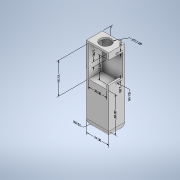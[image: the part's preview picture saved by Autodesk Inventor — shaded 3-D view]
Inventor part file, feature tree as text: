
AUTODESK INVENTOR PART (.ipt)
format: ipt  version: 2022.1 (Build 261234000, 234)  size: 217,088 bytes
history: native  units: mm
features: other x14, extrude x8, sketch x8, fillet x1
ambient origin geometry x8: Origin, YZ Plane, XZ Plane, XY Plane, X Axis, Y Axis, Z Axis, Center Point
bodies: Solid1 (feature_tree)
feature tree (31):
  other  "Annotations"
  extrude  "Extrusion1"  Depth=24.0mm
  extrude  "Extrusion2"  Depth=2.0mm
  extrude  "Extrusion3"  Depth=15.0mm TaperAngle=0.0deg
  extrude  "Extrusion4"  Depth=2.0mm
  extrude  "Extrusion5"  Depth=8.5mm
  extrude  "Extrusion6"  Depth=3.0mm
  fillet  "Fillet1"  Radius=12.0mm
  extrude  "Extrusion7"  Depth=23.5mm
  extrude  "Extrusion8"  Depth=2.0mm
  sketch  "Sketch1"  dims[d0=24.0mm d1=80.0mm]
  sketch  "Sketch2"  dims[d2=2.0mm d3=0.0mm d4=2.0mm]
  sketch  "Sketch3"  dims[d5=2.0mm d6=15.0mm d7=0.0mm]
  sketch  "Sketch4"  dims[d8=2.0mm d9=2.0mm]
  sketch  "Sketch5"  dims[d10=8.5mm d11=8.5mm]
  sketch  "Sketch6"  dims[d12=27.5mm d13=3.0mm d14=12.0mm d15=0.0mm]
  sketch  "Sketch7"  dims[d23=15.0mm d24=23.5mm]
  sketch  "Sketch8"  dims[d25=2.0mm d26=2.0mm d27=15.0mm d28=0.0mm d29=5.0mm d30=5.0mm d31=0.0mm d32=8.6mm d33=0.0mm d34=46.5mm d35=0.0mm d36=8.5mm d37=2.0mm d38=0.0mm d39=12.0mm d40=12.0mm d41=24.0mm d42=17.0mm d43=8.5mm d44=2.0mm d45=0.0mm d46=53.801048mm d47=6.030652mm d48=3.893802mm d49=8.5mm d50=3.768693mm d51=7.695168mm d52=73.5mm d53=0.0mm d54=10.0mm d55=17.0mm d56=0.0mm d57=10.0mm d58=24.0mm d59=42.144057mm d60=12.0mm d61=0.0mm d62=10.0mm d63=20.0mm d64=0.0mm d65=10.0mm d66=33.5mm d67=4.664241mm d68=4.459377mm d69=23.5mm d70=4.40635mm d71=2.0mm d72=0.553063mm d73=6.890367mm d74=2.0mm d75=61.44687mm d76=2.0mm d77=0.0mm d78=10.0mm d79=5.0mm d80=6.562561mm d81=2.37229mm d82=38.0mm]
  other  "Radial Dimension 1"
  other  "Linear Dimension 1"
  other  "Linear Dimension 2"
  other  "Linear Dimension 3"
  other  "Diameter Dimension 1"
  other  "Linear Dimension 4"
  other  "Linear Dimension 5"
  other  "Linear Dimension 6"
  other  "Linear Dimension 7"
  other  "Linear Dimension 8"
  other  "Diameter Dimension 2"
  other  "Linear Dimension 9"
  other  "Linear Dimension 10"
